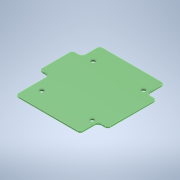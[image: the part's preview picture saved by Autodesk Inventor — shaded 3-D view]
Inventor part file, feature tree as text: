
AUTODESK INVENTOR PART (.ipt)
format: ipt  version: 2021 (Build 250183000, 183)  size: 178,688 bytes
history: native  units: mm
features: fillet x4, sketch x4, extrude x3, hole x1
ambient origin geometry x8: Origin, YZ Plane, XZ Plane, XY Plane, X Axis, Y Axis, Z Axis, Center Point
bodies: Solid1 (feature_tree)
feature tree (12):
  extrude  "Extrusion1"  Depth=95.0mm
  extrude  "Extrusion2"  Depth=11.0mm
  fillet  "Fillet1"  Radius=20.0mm
  fillet  "Fillet2"  Radius=20.0mm
  hole  "Hole2"  [1 undecoded]
  extrude  "Extrusion3"  Depth=11.0mm
  fillet  "Fillet3"  Radius=20.0mm
  fillet  "Fillet4"  Radius=1.6mm
  sketch  "Sketch1"  dims[d0=95.0mm d1=95.0mm]
  sketch  "Sketch4"  dims[d2=1.6mm d3=0.0mm d18=11.0mm d19=20.0mm d21=20.0mm]
  sketch  "Sketch6"  dims[d22=11.0mm d23=11.0mm]
  sketch  "Sketch7"  dims[d24=20.0mm d25=11.0mm d26=20.0mm d27=1.6mm d28=0.0mm d29=4.0mm d30=3.0mm d31=57.0mm d32=58.0mm d33=4.2mm d34=6.0mm d35=4.0mm d36=2.0mm d37=90.0deg d38=8.0mm d39=20.594885mm d41=3.0mm d43=10.0mm d44=0.0mm d45=22.0mm d46=3.0mm d47=4.0mm]
note: 1 required parameter value undecoded (feature->parameter linkage not recoverable at this tier; creation-order binding heuristic only, values carry confidence <= 0.55)
